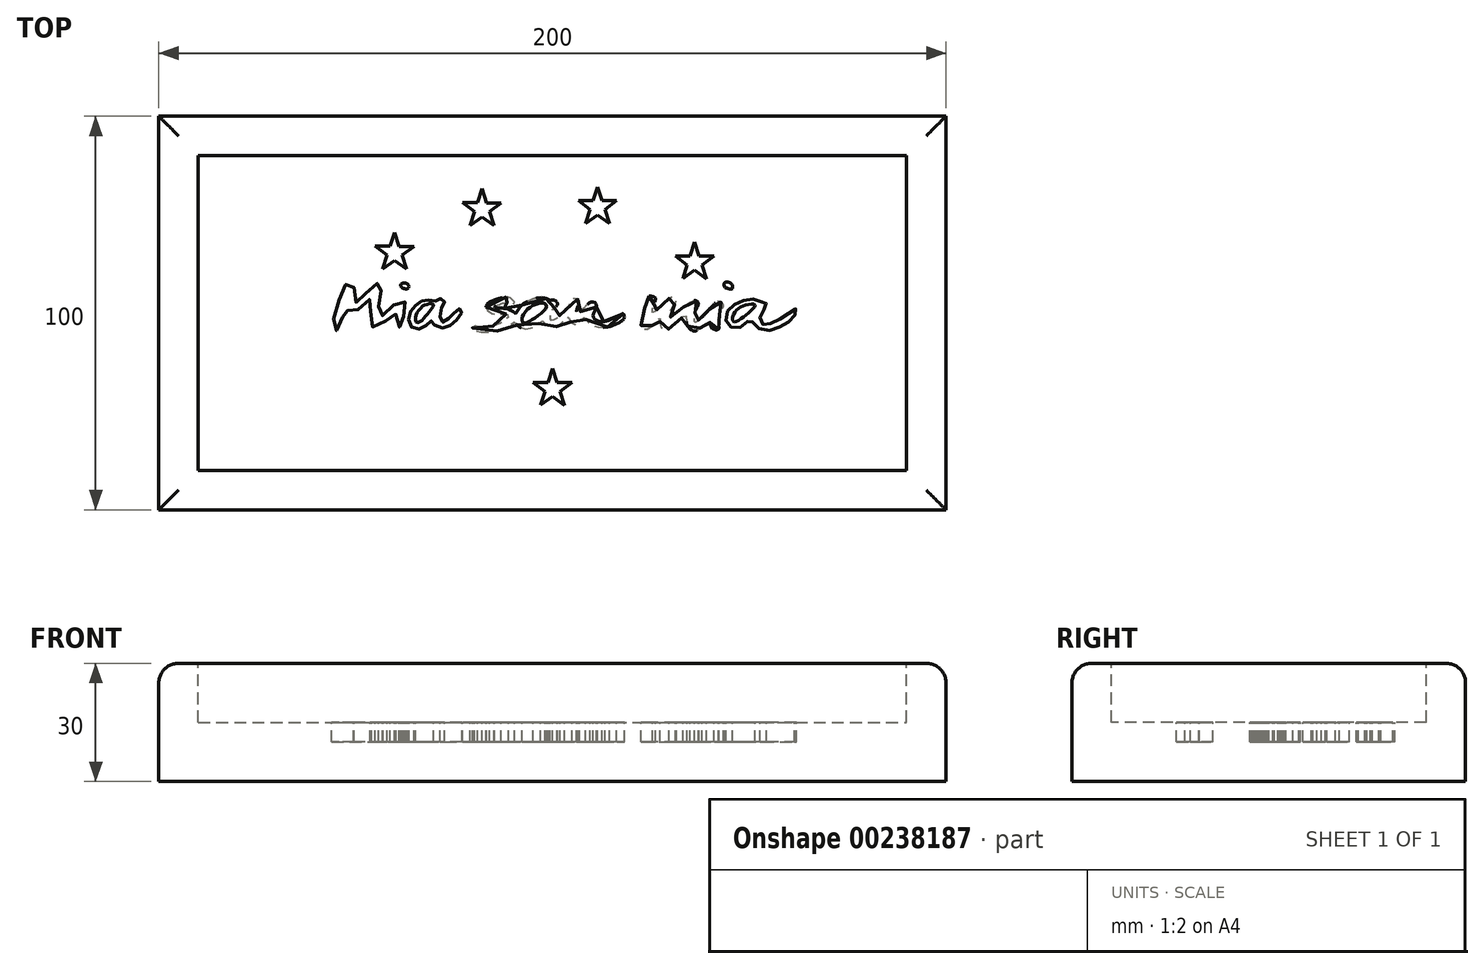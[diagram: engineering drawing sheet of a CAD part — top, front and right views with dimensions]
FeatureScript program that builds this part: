
annotation { "Feature Type Name" : "Feature", "Feature Type Description" : "" }
export const myFeature = defineFeature(function(context is Context, id is Id, definition is map)
    precondition{}
    {
        {
            var Q0;
            Q0=qCreatedBy(makeId("Top.planeOp"),FACE);
            var sketch = newSketch(context, id + "F0", { "sketchPlane" : qUnion([Q0])});
            skLineSegment(sketch, "E0", {"start": v(0, 0) * mm, "end": v(200, 0) * mm});
            skLineSegment(sketch, "E1", {"start": v(0, 0) * mm, "end": v(0, 100) * mm});
            skLineSegment(sketch, "E2", {"start": v(0, 100) * mm, "end": v(200, 100) * mm});
            skLineSegment(sketch, "E3", {"start": v(200, 100) * mm, "end": v(200, 0) * mm});
            skSolve(sketch);
        }
        {
            var Q0;
            Q0=makeQuery(id+"F0.imprint","IMPRINT",FACE,{"disambiguationData":[TD([[makeQuery(id+"F0.imprint","IMPRINT",EDGE,{"derivedFrom":sQuery(id+"F0.wireOp",EDGE,"E0")}),1.0]])]});
            extrude(context, id + "F1", {"entities" : qUnion([Q0]), "depth" : 30 * mm});
        }
        {
            var Q0;
            Q0=makeQuery(id+"F1.opExtrude","CAP_FACE",FACE,{"disambiguationData":[OSD([sQuery(id+"F0.wireOp",EDGE,"E0"),sQuery(id+"F0.wireOp",EDGE,"E1"),sQuery(id+"F0.wireOp",EDGE,"E2"),sQuery(id+"F0.wireOp",EDGE,"E3")])],"isStart":false});
            var sketch = newSketch(context, id + "F2", { "sketchPlane" : qUnion([Q0])});
            skLineSegment(sketch, "E4", {"start": v(10, 10) * mm, "end": v(190, 10) * mm});
            skLineSegment(sketch, "E5", {"start": v(190, 10) * mm, "end": v(190, 90) * mm});
            skLineSegment(sketch, "E6", {"start": v(190, 90) * mm, "end": v(10, 90) * mm});
            skLineSegment(sketch, "E7", {"start": v(10, 90) * mm, "end": v(10, 10) * mm});
            skSolve(sketch);
        }
        {
            var Q0;
            Q0=makeQuery(id+"F2.imprint","IMPRINT",FACE,{"disambiguationData":[TD([[makeQuery(id+"F2.imprint","IMPRINT",EDGE,{"derivedFrom":sQuery(id+"F2.wireOp",EDGE,"E4")}),1.0]])]});
            extrude(context, id + "F3", {"entities" : qUnion([Q0]), "operationType" : NewBodyOperationType.REMOVE, "oppositeDirection" : true, "depth" : 15 * mm});
        }
        {
            var Q0;
            Q0=makeQuery(id+"F1.opExtrude","CAP_EDGE",EDGE,{"disambiguationData":[OSD([sQuery(id+"F0.wireOp",EDGE,"E1")])],"isStart":false});
            var Q1;
            Q1=makeQuery(id+"F3.boolean.opBoolean","COPY",EDGE,{"derivedFrom":makeQuery(id+"F3.opExtrude","CAP_EDGE",EDGE,{"disambiguationData":[OSD([sQuery(id+"F2.wireOp",EDGE,"E7")])],"isStart":true})});
            var Q2;
            Q2=makeQuery(id+"F3.boolean.opBoolean","COPY",EDGE,{"derivedFrom":makeQuery(id+"F3.opExtrude","CAP_EDGE",EDGE,{"disambiguationData":[OSD([sQuery(id+"F2.wireOp",EDGE,"E6")])],"isStart":true})});
            var Q3;
            Q3=makeQuery(id+"F1.opExtrude","CAP_EDGE",EDGE,{"disambiguationData":[OSD([sQuery(id+"F0.wireOp",EDGE,"E2")])],"isStart":false});
            var Q4;
            Q4=makeQuery(id+"F1.opExtrude","CAP_EDGE",EDGE,{"disambiguationData":[OSD([sQuery(id+"F0.wireOp",EDGE,"E3")])],"isStart":false});
            var Q5;
            Q5=makeQuery(id+"F3.boolean.opBoolean","COPY",EDGE,{"derivedFrom":makeQuery(id+"F3.opExtrude","CAP_EDGE",EDGE,{"disambiguationData":[OSD([sQuery(id+"F2.wireOp",EDGE,"E5")])],"isStart":true})});
            var Q6;
            Q6=makeQuery(id+"F3.boolean.opBoolean","COPY",EDGE,{"derivedFrom":makeQuery(id+"F3.opExtrude","CAP_EDGE",EDGE,{"disambiguationData":[OSD([sQuery(id+"F2.wireOp",EDGE,"E4")])],"isStart":true})});
            var Q7;
            Q7=makeQuery(id+"F1.opExtrude","CAP_EDGE",EDGE,{"disambiguationData":[OSD([sQuery(id+"F0.wireOp",EDGE,"E0")])],"isStart":false});
            fillet(context, id + "F4", {"entities" : qUnion([Q0, Q1, Q2, Q3, Q4, Q5, Q6, Q7]), "radius" : 5 * mm, "tangentPropagation" : true, "allowEdgeOverflow" : false});
        }
        {
            var Q0;
            Q0=makeQuery(id+"F3.boolean.opBoolean","COPY",FACE,{"derivedFrom":makeQuery(id+"F3.opExtrude","CAP_FACE",FACE,{"disambiguationData":[OSD([sQuery(id+"F2.wireOp",EDGE,"E4"),sQuery(id+"F2.wireOp",EDGE,"E5"),sQuery(id+"F2.wireOp",EDGE,"E6"),sQuery(id+"F2.wireOp",EDGE,"E7")])],"isStart":false})});
            var sketch = newSketch(context, id + "F5", { "sketchPlane" : qUnion([Q0])});
            skFitSpline(sketch, "E8", {"points": [v(45.86, 53.28) * mm, v(45.29, 51.76) * mm, v(44.75, 49.78) * mm, v(44.34, 48.26) * mm, v(44.05, 46.94) * mm, v(43.93, 46.12) * mm, v(44.38, 45.67) * mm, v(45.33, 45.54) * mm, v(45.9, 45.8) * mm, v(46.2, 47.03) * mm, v(46.52, 48.38) * mm, v(46.8, 49.62) * mm, v(47.18, 50.9) * mm, v(47.39, 51.35) * mm, v(47.71, 51.27) * mm, v(48, 50.44) * mm, v(48.46, 49.99) * mm, v(49.16, 49.83) * mm, v(49.94, 50.03) * mm, v(50.6, 50.77) * mm, v(51.46, 51.55) * mm, v(52.33, 52.42) * mm, v(52.94, 53) * mm, v(53.56, 53.49) * mm, v(53.9, 53.65) * mm, v(54.01, 52.91) * mm, v(53.93, 51.72) * mm, v(53.85, 50.44) * mm, v(53.77, 49.08) * mm, v(53.68, 47.56) * mm, v(53.93, 46.78) * mm, v(54.6, 46.33) * mm, v(55.58, 46.37) * mm, v(56.28, 46.74) * mm, v(57.27, 47.6) * mm, v(57.92, 48.34) * mm, v(58.75, 49.04) * mm, v(59.49, 49.7) * mm, v(59.86, 49.87) * mm, v(60.19, 49.66) * mm, v(60.23, 48.3) * mm, v(60.23, 47.4) * mm, v(60.56, 46.78) * mm, v(61.18, 46.4) * mm, v(62, 46.45) * mm, v(62.41, 46.98) * mm, v(62.33, 47.97) * mm, v(62.2, 49) * mm, v(62.29, 50.28) * mm, v(62.37, 51.27) * mm, v(62.45, 52.05) * mm, v(62.5, 52.87) * mm, v(62, 53.28) * mm, v(61.22, 53.28) * mm, v(60.52, 52.95) * mm, v(59.65, 52.05) * mm, v(58.91, 51.35) * mm, v(58.13, 50.6) * mm, v(57.3, 49.74) * mm, v(56.73, 49.25) * mm, v(56.24, 48.92) * mm, v(55.9, 49) * mm, v(55.87, 50.15) * mm, v(55.87, 51.51) * mm, v(55.9, 52.75) * mm, v(55.99, 53.98) * mm, v(56.24, 55.14) * mm, v(56.65, 56.08) * mm, v(56.98, 56.66) * mm, v(56.81, 57.24) * mm, v(56.32, 57.52) * mm, v(55.66, 57.56) * mm, v(55.04, 57.15) * mm, v(54.34, 56.54) * mm, v(53.48, 55.63) * mm, v(52.66, 55.05) * mm, v(51.87, 54.19) * mm, v(51.17, 53.53) * mm, v(50.72, 53) * mm, v(50.27, 52.75) * mm, v(50.02, 52.7) * mm, v(49.57, 53.2) * mm, v(49.49, 54.77) * mm, v(49.57, 55.96) * mm, v(49.6, 57.15) * mm, v(49.32, 57.73) * mm, v(48.79, 58.02) * mm, v(48, 57.9) * mm, v(47.26, 56.74) * mm, v(46.85, 55.8) * mm, v(46.36, 54.72) * mm, v(45.86, 53.28) * mm]});
            skFitSpline(sketch, "E9", {"points": [v(62.17, 57.65) * mm, v(61.67, 57.44) * mm, v(61.47, 56.78) * mm, v(62, 56.33) * mm, v(62.78, 56.12) * mm, v(63.44, 56.37) * mm, v(63.52, 56.9) * mm, v(63.07, 57.44) * mm, v(62.17, 57.65) * mm]});
            skFitSpline(sketch, "E10", {"points": [v(66.53, 51.18) * mm, v(65.79, 50.32) * mm, v(65.38, 49.33) * mm, v(65.21, 48.6) * mm, v(65.34, 47.9) * mm, v(65.7, 47.56) * mm, v(66.36, 47.8) * mm, v(67.02, 48.3) * mm, v(67.85, 49.29) * mm, v(68.46, 49.95) * mm, v(69.08, 50.81) * mm, v(69.62, 51.47) * mm, v(69.78, 51.88) * mm, v(69.66, 52.3) * mm, v(68.96, 52.38) * mm, v(68.01, 52.17) * mm, v(67.31, 51.92) * mm, v(66.53, 51.18) * mm]});
            skFitSpline(sketch, "E11", {"points": [v(65.3, 51.92) * mm, v(64.47, 51.18) * mm, v(63.85, 50.11) * mm, v(63.52, 48.96) * mm, v(63.56, 47.68) * mm, v(63.98, 46.66) * mm, v(64.84, 46) * mm, v(66.16, 45.87) * mm, v(67.31, 46.2) * mm, v(68.05, 47.03) * mm, v(68.8, 47.68) * mm, v(69.2, 48.01) * mm, v(69.53, 48.01) * mm, v(69.82, 47.2) * mm, v(70.69, 46.61) * mm, v(72.05, 46.2) * mm, v(73.24, 46.4) * mm, v(74.19, 46.86) * mm, v(75.1, 47.64) * mm, v(75.96, 48.67) * mm, v(76.78, 49.78) * mm, v(77.03, 50.65) * mm, v(76.74, 51.06) * mm, v(76.2, 51.02) * mm, v(75.34, 50.32) * mm, v(74.64, 49.54) * mm, v(74.06, 49.08) * mm, v(73.36, 48.38) * mm, v(72.62, 47.93) * mm, v(71.96, 47.68) * mm, v(71.55, 48.18) * mm, v(71.47, 49.29) * mm, v(71.68, 50.69) * mm, v(72.09, 51.92) * mm, v(72.54, 52.46) * mm, v(72.62, 52.87) * mm, v(72.42, 53.28) * mm, v(71.8, 53.57) * mm, v(71.18, 53.65) * mm, v(70.6, 53.28) * mm, v(70.28, 53.08) * mm, v(69.66, 53.28) * mm, v(68.5, 53.28) * mm, v(67.93, 53.28) * mm, v(66.86, 53.04) * mm, v(66, 52.62) * mm, v(65.3, 51.92) * mm]});
            skFitSpline(sketch, "E12", {"points": [v(83.18, 51.54) * mm, v(83.26, 50.92) * mm, v(83.96, 50.18) * mm, v(85.03, 49.77) * mm, v(86.35, 49.69) * mm, v(87.58, 49.77) * mm, v(88.36, 49.69) * mm, v(88.86, 49.48) * mm, v(88.65, 48.78) * mm, v(88, 48.2) * mm, v(87.13, 47.59) * mm, v(86.22, 47.1) * mm, v(84.5, 46.56) * mm, v(83.34, 46.44) * mm, v(82.06, 46.4) * mm, v(81.16, 46.4) * mm, v(80.79, 46.6) * mm, v(80.25, 46.68) * mm, v(79.68, 46.27) * mm, v(80, 45.65) * mm, v(80.83, 45.32) * mm, v(82.06, 45.16) * mm, v(83.67, 45.16) * mm, v(85.52, 45.37) * mm, v(87.09, 45.82) * mm, v(88.16, 46.27) * mm, v(89.35, 46.93) * mm, v(90.13, 47.67) * mm, v(90.34, 47.8) * mm, v(90.96, 47.05) * mm, v(91.66, 46.44) * mm, v(92.77, 45.98) * mm, v(93.67, 45.94) * mm, v(94.9, 46.31) * mm, v(95.98, 46.89) * mm, v(96.93, 47.63) * mm, v(97.46, 47.96) * mm, v(97.83, 47.84) * mm, v(98.24, 47.14) * mm, v(99.07, 46.72) * mm, v(100.01, 46.44) * mm, v(100.92, 46.48) * mm, v(101.87, 47.14) * mm, v(102.6, 47.8) * mm, v(103.22, 48.5) * mm, v(103.76, 49.03) * mm, v(104.09, 49.07) * mm, v(104.38, 48.04) * mm, v(105.2, 47.3) * mm, v(105.94, 47.1) * mm, v(106.52, 47.47) * mm, v(107.05, 48) * mm, v(107.59, 48.54) * mm, v(108.08, 48.82) * mm, v(108.54, 48.45) * mm, v(109.11, 47.67) * mm, v(109.81, 47.1) * mm, v(110.92, 46.56) * mm, v(111.75, 46.4) * mm, v(113.02, 46.35) * mm, v(114.5, 46.56) * mm, v(115.7, 46.97) * mm, v(116.9, 47.55) * mm, v(117.8, 48.17) * mm, v(118.25, 48.74) * mm, v(118.13, 49.6) * mm, v(117.84, 49.98) * mm, v(117.47, 49.81) * mm, v(116.81, 49.28) * mm, v(115.74, 48.74) * mm, v(114.67, 48.25) * mm, v(113.6, 47.96) * mm, v(112.65, 47.8) * mm, v(111.62, 47.96) * mm, v(110.72, 48.45) * mm, v(110.35, 49.15) * mm, v(110.55, 50.06) * mm, v(111.09, 51.13) * mm, v(111.25, 51.87) * mm, v(110.88, 52.57) * mm, v(110.02, 52.82) * mm, v(109.11, 52.36) * mm, v(108.17, 51.42) * mm, v(107.3, 50.55) * mm, v(106.64, 49.48) * mm, v(106.19, 49.9) * mm, v(106.23, 50.96) * mm, v(106.6, 51.95) * mm, v(106.89, 52.74) * mm, v(106.6, 53.35) * mm, v(106.07, 53.6) * mm, v(105.12, 53.52) * mm, v(104.46, 52.4) * mm, v(103.51, 51.09) * mm, v(102.48, 49.98) * mm, v(101.2, 48.7) * mm, v(99.97, 48.08) * mm, v(99.52, 48.41) * mm, v(99.52, 49.44) * mm, v(99.8, 50.39) * mm, v(100.3, 51.13) * mm, v(100.92, 51.66) * mm, v(101.29, 52.16) * mm, v(101.04, 52.9) * mm, v(100.43, 53.27) * mm, v(99.8, 53.27) * mm, v(99.4, 53.19) * mm, v(98.61, 53.6) * mm, v(97.63, 53.85) * mm, v(96.43, 53.8) * mm, v(95, 53.52) * mm, v(94.2, 53.15) * mm, v(92.9, 52.53) * mm, v(91.7, 51.34) * mm, v(90.96, 50.3) * mm, v(90.67, 49.9) * mm, v(90.1, 50.3) * mm, v(89.1, 50.8) * mm, v(88, 51.13) * mm, v(86.67, 51.21) * mm, v(85.6, 51.3) * mm, v(85.36, 51.58) * mm, v(86.22, 52.08) * mm, v(87.3, 52.45) * mm, v(88.36, 52.65) * mm, v(88.94, 52.61) * mm, v(89.43, 52.32) * mm, v(90.05, 52.32) * mm, v(90.38, 52.65) * mm, v(90, 53.15) * mm, v(89.47, 53.72) * mm, v(88.45, 54.01) * mm, v(87.42, 53.93) * mm, v(86.14, 53.6) * mm, v(85.2, 53.27) * mm, v(84.16, 52.82) * mm, v(83.5, 52.36) * mm, v(83.18, 51.54) * mm]});
            skFitSpline(sketch, "E13", {"points": [v(95, 51.83) * mm, v(93.92, 51.09) * mm, v(92.77, 49.9) * mm, v(92.27, 48.62) * mm, v(92.32, 47.8) * mm, v(92.73, 47.5) * mm, v(94.13, 47.8) * mm, v(95.03, 48.41) * mm, v(96.64, 49.48) * mm, v(97.8, 50.55) * mm, v(98.5, 51.62) * mm, v(98.2, 52.32) * mm, v(97.26, 52.57) * mm, v(96.4, 52.36) * mm, v(95, 51.83) * mm]});
            skFitSpline(sketch, "E14", {"points": [v(124.6, 54.3) * mm, v(124.22, 54.1) * mm, v(124.14, 53.44) * mm, v(123.85, 52.28) * mm, v(123.36, 50.8) * mm, v(122.9, 49.32) * mm, v(122.53, 47.96) * mm, v(122.57, 46.48) * mm, v(123.1, 45.94) * mm, v(124.22, 45.9) * mm, v(125.13, 46.68) * mm, v(126.24, 47.84) * mm, v(126.86, 48.45) * mm, v(127.27, 48.62) * mm, v(127.35, 47.63) * mm, v(127.56, 46.48) * mm, v(128.05, 45.9) * mm, v(129.2, 45.74) * mm, v(130.1, 46.4) * mm, v(131.38, 47.5) * mm, v(132.46, 48.41) * mm, v(133.36, 49.2) * mm, v(133.9, 49.28) * mm, v(134.1, 47.55) * mm, v(134.55, 46.44) * mm, v(135.5, 45.57) * mm, v(136.7, 45.53) * mm, v(137.44, 46.1) * mm, v(138.59, 47.01) * mm, v(139.45, 47.84) * mm, v(139.82, 48.08) * mm, v(140.11, 47.3) * mm, v(140.4, 46.27) * mm, v(141.14, 45.82) * mm, v(141.92, 45.74) * mm, v(142.34, 46.19) * mm, v(142.25, 47.05) * mm, v(142.17, 48.29) * mm, v(142.42, 49.48) * mm, v(142.91, 50.84) * mm, v(143.4, 51.54) * mm, v(143.24, 52.45) * mm, v(142.42, 52.86) * mm, v(141.76, 52.86) * mm, v(140.81, 51.83) * mm, v(139.95, 50.96) * mm, v(139.08, 50.06) * mm, v(138.22, 49.15) * mm, v(137.23, 48.29) * mm, v(136.65, 47.75) * mm, v(136.2, 47.67) * mm, v(136.08, 48.74) * mm, v(136.24, 50.02) * mm, v(136.61, 51.09) * mm, v(137.03, 52.12) * mm, v(136.98, 52.74) * mm, v(136.49, 53.1) * mm, v(135.83, 53.1) * mm, v(134.68, 52.36) * mm, v(133.6, 51.7) * mm, v(132.66, 50.8) * mm, v(131.34, 49.98) * mm, v(130.23, 49.07) * mm, v(129.66, 48.82) * mm, v(129.7, 49.69) * mm, v(130.52, 51.38) * mm, v(131.38, 52.65) * mm, v(131.38, 53.48) * mm, v(130.8, 53.93) * mm, v(129.86, 53.85) * mm, v(128.83, 53.02) * mm, v(127.8, 51.87) * mm, v(126.77, 51) * mm, v(125.83, 50.22) * mm, v(125.5, 50.1) * mm, v(125.5, 51.05) * mm, v(125.87, 52.32) * mm, v(126.07, 52.98) * mm, v(126.16, 53.8) * mm, v(125.42, 54.18) * mm, v(124.6, 54.3) * mm]});
            skFitSpline(sketch, "E15", {"points": [v(147.28, 51.16) * mm, v(146.52, 50.43) * mm, v(145.9, 49.41) * mm, v(145.8, 48.29) * mm, v(146.11, 47.72) * mm, v(146.9, 47.93) * mm, v(148.03, 48.68) * mm, v(149.17, 49.47) * mm, v(150.33, 50.49) * mm, v(151.12, 51.27) * mm, v(151.47, 51.86) * mm, v(151.32, 52.2) * mm, v(150.36, 52.2) * mm, v(149.1, 51.97) * mm, v(148.1, 51.57) * mm, v(147.28, 51.16) * mm]});
            skFitSpline(sketch, "E16", {"points": [v(146.26, 52.2) * mm, v(145.27, 51.42) * mm, v(144.3, 50.06) * mm, v(144.07, 48.8) * mm, v(144.25, 47.43) * mm, v(144.95, 46.65) * mm, v(145.94, 46.15) * mm, v(147.28, 46.15) * mm, v(148.56, 47.05) * mm, v(149.46, 47.78) * mm, v(150.16, 48.29) * mm, v(150.5, 48.29) * mm, v(151.03, 47.37) * mm, v(151.85, 46.41) * mm, v(153.16, 45.77) * mm, v(154.87, 45.57) * mm, v(156.5, 45.92) * mm, v(158.02, 46.59) * mm, v(159.44, 47.37) * mm, v(160.7, 48.29) * mm, v(161.6, 49.32) * mm, v(161.57, 49.98) * mm, v(161.98, 50.37) * mm, v(161.57, 51.16) * mm, v(160.78, 50.52) * mm, v(159.59, 49.64) * mm, v(158.22, 48.74) * mm, v(156.53, 47.8) * mm, v(155.28, 47.34) * mm, v(154.44, 47.05) * mm, v(153.62, 47.05) * mm, v(152.86, 47.7) * mm, v(152.7, 48.57) * mm, v(152.86, 49.61) * mm, v(153.6, 50.75) * mm, v(154.3, 51.54) * mm, v(154.4, 52.09) * mm, v(154.15, 52.67) * mm, v(153.6, 53) * mm, v(153.07, 52.96) * mm, v(152.43, 53.02) * mm, v(151.58, 53.43) * mm, v(150.3, 53.49) * mm, v(148.96, 53.31) * mm, v(147.71, 52.9) * mm, v(146.26, 52.2) * mm]});
            skFitSpline(sketch, "E17", {"points": [v(143.6, 57.36) * mm, v(143.9, 57.8) * mm, v(144.8, 57.82) * mm, v(145.59, 57.27) * mm, v(145.8, 56.6) * mm, v(145.59, 56.1) * mm, v(144.71, 56.2) * mm, v(143.84, 56.51) * mm, v(143.6, 57.36) * mm]});
            skSolve(sketch);
        }
        {
            var Q0;
            Q0=makeQuery(id+"F5.imprint","IMPRINT",FACE,{"disambiguationData":[TD([[makeQuery(id+"F5.imprint","IMPRINT",EDGE,{"derivedFrom":sQuery(id+"F5.wireOp",EDGE,"E8")}),1.0]])]});
            var Q1;
            Q1=makeQuery(id+"F5.imprint","IMPRINT",FACE,{"disambiguationData":[TD([[makeQuery(id+"F5.imprint","IMPRINT",EDGE,{"derivedFrom":sQuery(id+"F5.wireOp",EDGE,"E10")}),-1.0]])]});
            var Q2;
            Q2=makeQuery(id+"F5.imprint","IMPRINT",FACE,{"disambiguationData":[TD([[makeQuery(id+"F5.imprint","IMPRINT",EDGE,{"derivedFrom":sQuery(id+"F5.wireOp",EDGE,"E9")}),1.0]])]});
            var Q3;
            Q3=makeQuery(id+"F5.imprint","IMPRINT",FACE,{"disambiguationData":[TD([[makeQuery(id+"F5.imprint","IMPRINT",EDGE,{"derivedFrom":sQuery(id+"F5.wireOp",EDGE,"E12")}),1.0]])]});
            var Q4;
            Q4=makeQuery(id+"F5.imprint","IMPRINT",FACE,{"disambiguationData":[TD([[makeQuery(id+"F5.imprint","IMPRINT",EDGE,{"derivedFrom":sQuery(id+"F5.wireOp",EDGE,"E14")}),1.0]])]});
            var Q5;
            Q5=makeQuery(id+"F5.imprint","IMPRINT",FACE,{"disambiguationData":[TD([[makeQuery(id+"F5.imprint","IMPRINT",EDGE,{"derivedFrom":sQuery(id+"F5.wireOp",EDGE,"E15")}),-1.0]])]});
            var Q6;
            Q6=makeQuery(id+"F5.imprint","IMPRINT",FACE,{"disambiguationData":[TD([[makeQuery(id+"F5.imprint","IMPRINT",EDGE,{"derivedFrom":sQuery(id+"F5.wireOp",EDGE,"E17")}),-1.0]])]});
            extrude(context, id + "F6", {"entities" : qUnion([Q0, Q1, Q2, Q3, Q4, Q5, Q6]), "operationType" : NewBodyOperationType.REMOVE, "oppositeDirection" : true, "depth" : 5 * mm});
        }
        {
            var Q0;
            {var subQ0=sQuery(id+"F2.wireOp",EDGE,"E7");var subQ1=sQuery(id+"F2.wireOp",EDGE,"E4");var subQ2=sQuery(id+"F2.wireOp",EDGE,"E5");var subQ3=sQuery(id+"F2.wireOp",EDGE,"E6");Q0=makeQuery(id+"F6.boolean.opBoolean","SPLIT",FACE,{"disambiguationData":[TD([makeQuery(id+"F3.boolean.opBoolean","COPY",FACE,{"derivedFrom":makeQuery(id+"F3.opExtrude","SWEPT_FACE",FACE,{"disambiguationData":[OSD([subQ1])]})})])],"derivedFrom":makeQuery(id+"F3.boolean.opBoolean","COPY",FACE,{"derivedFrom":makeQuery(id+"F3.opExtrude","CAP_FACE",FACE,{"disambiguationData":[OSD([subQ1,subQ2,subQ3,subQ0])],"isStart":false})})});}
            var sketch = newSketch(context, id + "F7", { "sketchPlane" : qUnion([Q0])});
            skLineSegment(sketch, "E18", {"start": v(59.93, 70.5) * mm, "end": v(61.06, 66.92) * mm});
            skLineSegment(sketch, "E19", {"start": v(61.06, 66.92) * mm, "end": v(64.81, 66.92) * mm});
            skLineSegment(sketch, "E20", {"start": v(64.81, 66.92) * mm, "end": v(61.78, 64.75) * mm});
            skLineSegment(sketch, "E21", {"start": v(61.78, 64.75) * mm, "end": v(62.94, 61.16) * mm});
            skLineSegment(sketch, "E22", {"start": v(62.94, 61.16) * mm, "end": v(59.92, 63.36) * mm});
            skLineSegment(sketch, "E23", {"start": v(59.92, 63.36) * mm, "end": v(56.89, 61.17) * mm});
            skLineSegment(sketch, "E24", {"start": v(56.89, 61.17) * mm, "end": v(58.02, 64.7) * mm});
            skLineSegment(sketch, "E25", {"start": v(58.02, 64.7) * mm, "end": v(55, 66.94) * mm});
            skLineSegment(sketch, "E26", {"start": v(55, 66.94) * mm, "end": v(58.73, 66.94) * mm});
            skLineSegment(sketch, "E27", {"start": v(58.73, 66.94) * mm, "end": v(59.93, 70.5) * mm});
            skLineSegment(sketch, "E28", {"start": v(82.14, 81.56) * mm, "end": v(83.32, 77.96) * mm});
            skLineSegment(sketch, "E29", {"start": v(83.32, 77.96) * mm, "end": v(87, 77.96) * mm});
            skLineSegment(sketch, "E30", {"start": v(87, 77.96) * mm, "end": v(84.01, 75.83) * mm});
            skLineSegment(sketch, "E31", {"start": v(84.01, 75.83) * mm, "end": v(85.17, 72.2) * mm});
            skLineSegment(sketch, "E32", {"start": v(85.17, 72.2) * mm, "end": v(82.15, 74.42) * mm});
            skLineSegment(sketch, "E33", {"start": v(82.15, 74.42) * mm, "end": v(79.13, 72.26) * mm});
            skLineSegment(sketch, "E34", {"start": v(79.13, 72.26) * mm, "end": v(80.26, 75.8) * mm});
            skLineSegment(sketch, "E35", {"start": v(80.26, 75.8) * mm, "end": v(77.22, 78) * mm});
            skLineSegment(sketch, "E36", {"start": v(77.22, 78) * mm, "end": v(80.96, 78) * mm});
            skLineSegment(sketch, "E37", {"start": v(80.96, 78) * mm, "end": v(82.14, 81.56) * mm});
            skLineSegment(sketch, "E38", {"start": v(111.45, 82.04) * mm, "end": v(112.61, 78.5) * mm});
            skLineSegment(sketch, "E39", {"start": v(112.61, 78.5) * mm, "end": v(116.33, 78.5) * mm});
            skLineSegment(sketch, "E40", {"start": v(116.33, 78.5) * mm, "end": v(113.36, 76.34) * mm});
            skLineSegment(sketch, "E41", {"start": v(113.36, 76.34) * mm, "end": v(114.46, 72.74) * mm});
            skLineSegment(sketch, "E42", {"start": v(114.46, 72.74) * mm, "end": v(111.47, 74.9) * mm});
            skLineSegment(sketch, "E43", {"start": v(111.47, 74.9) * mm, "end": v(108.4, 72.76) * mm});
            skLineSegment(sketch, "E44", {"start": v(108.4, 72.76) * mm, "end": v(109.57, 76.25) * mm});
            skLineSegment(sketch, "E45", {"start": v(109.57, 76.25) * mm, "end": v(106.6, 78.5) * mm});
            skLineSegment(sketch, "E46", {"start": v(106.6, 78.5) * mm, "end": v(110.32, 78.5) * mm});
            skLineSegment(sketch, "E47", {"start": v(110.32, 78.5) * mm, "end": v(111.45, 82.04) * mm});
            skLineSegment(sketch, "E48", {"start": v(136.13, 68) * mm, "end": v(137.3, 64.41) * mm});
            skLineSegment(sketch, "E49", {"start": v(137.3, 64.41) * mm, "end": v(141.02, 64.41) * mm});
            skLineSegment(sketch, "E50", {"start": v(141.02, 64.41) * mm, "end": v(138.01, 62.22) * mm});
            skLineSegment(sketch, "E51", {"start": v(138.01, 62.22) * mm, "end": v(139.17, 58.62) * mm});
            skLineSegment(sketch, "E52", {"start": v(139.17, 58.62) * mm, "end": v(136.15, 60.86) * mm});
            skLineSegment(sketch, "E53", {"start": v(136.15, 60.86) * mm, "end": v(133.15, 58.7) * mm});
            skLineSegment(sketch, "E54", {"start": v(133.15, 58.7) * mm, "end": v(134.26, 62.19) * mm});
            skLineSegment(sketch, "E55", {"start": v(134.26, 62.19) * mm, "end": v(131.25, 64.41) * mm});
            skLineSegment(sketch, "E56", {"start": v(131.25, 64.41) * mm, "end": v(134.96, 64.41) * mm});
            skLineSegment(sketch, "E57", {"start": v(134.96, 64.41) * mm, "end": v(136.13, 68) * mm});
            skLineSegment(sketch, "E58", {"start": v(100.06, 35.84) * mm, "end": v(101.24, 32.31) * mm});
            skLineSegment(sketch, "E59", {"start": v(101.24, 32.31) * mm, "end": v(104.92, 32.31) * mm});
            skLineSegment(sketch, "E60", {"start": v(104.92, 32.31) * mm, "end": v(101.97, 30.1) * mm});
            skLineSegment(sketch, "E61", {"start": v(101.97, 30.1) * mm, "end": v(103.12, 26.52) * mm});
            skLineSegment(sketch, "E62", {"start": v(103.12, 26.52) * mm, "end": v(100.08, 28.75) * mm});
            skLineSegment(sketch, "E63", {"start": v(100.08, 28.75) * mm, "end": v(97.05, 26.58) * mm});
            skLineSegment(sketch, "E64", {"start": v(97.05, 26.58) * mm, "end": v(98.19, 30.07) * mm});
            skLineSegment(sketch, "E65", {"start": v(98.19, 30.07) * mm, "end": v(95.14, 32.3) * mm});
            skLineSegment(sketch, "E66", {"start": v(95.14, 32.3) * mm, "end": v(98.88, 32.3) * mm});
            skLineSegment(sketch, "E67", {"start": v(98.88, 32.3) * mm, "end": v(100.06, 35.84) * mm});
            skSolve(sketch);
        }
        {
            var Q0;
            Q0=makeQuery(id+"F7.imprint","IMPRINT",FACE,{"disambiguationData":[TD([[makeQuery(id+"F7.imprint","IMPRINT",EDGE,{"derivedFrom":sQuery(id+"F7.wireOp",EDGE,"E58")}),-1.0]])]});
            var Q1;
            Q1=makeQuery(id+"F7.imprint","IMPRINT",FACE,{"disambiguationData":[TD([[makeQuery(id+"F7.imprint","IMPRINT",EDGE,{"derivedFrom":sQuery(id+"F7.wireOp",EDGE,"E18")}),-1.0]])]});
            var Q2;
            Q2=makeQuery(id+"F7.imprint","IMPRINT",FACE,{"disambiguationData":[TD([[makeQuery(id+"F7.imprint","IMPRINT",EDGE,{"derivedFrom":sQuery(id+"F7.wireOp",EDGE,"E28")}),-1.0]])]});
            var Q3;
            Q3=makeQuery(id+"F7.imprint","IMPRINT",FACE,{"disambiguationData":[TD([[makeQuery(id+"F7.imprint","IMPRINT",EDGE,{"derivedFrom":sQuery(id+"F7.wireOp",EDGE,"E38")}),-1.0]])]});
            var Q4;
            Q4=makeQuery(id+"F7.imprint","IMPRINT",FACE,{"disambiguationData":[TD([[makeQuery(id+"F7.imprint","IMPRINT",EDGE,{"derivedFrom":sQuery(id+"F7.wireOp",EDGE,"E48")}),-1.0]])]});
            extrude(context, id + "F8", {"entities" : qUnion([Q0, Q1, Q2, Q3, Q4]), "operationType" : NewBodyOperationType.REMOVE, "oppositeDirection" : true, "depth" : 5 * mm});
        }
    });
